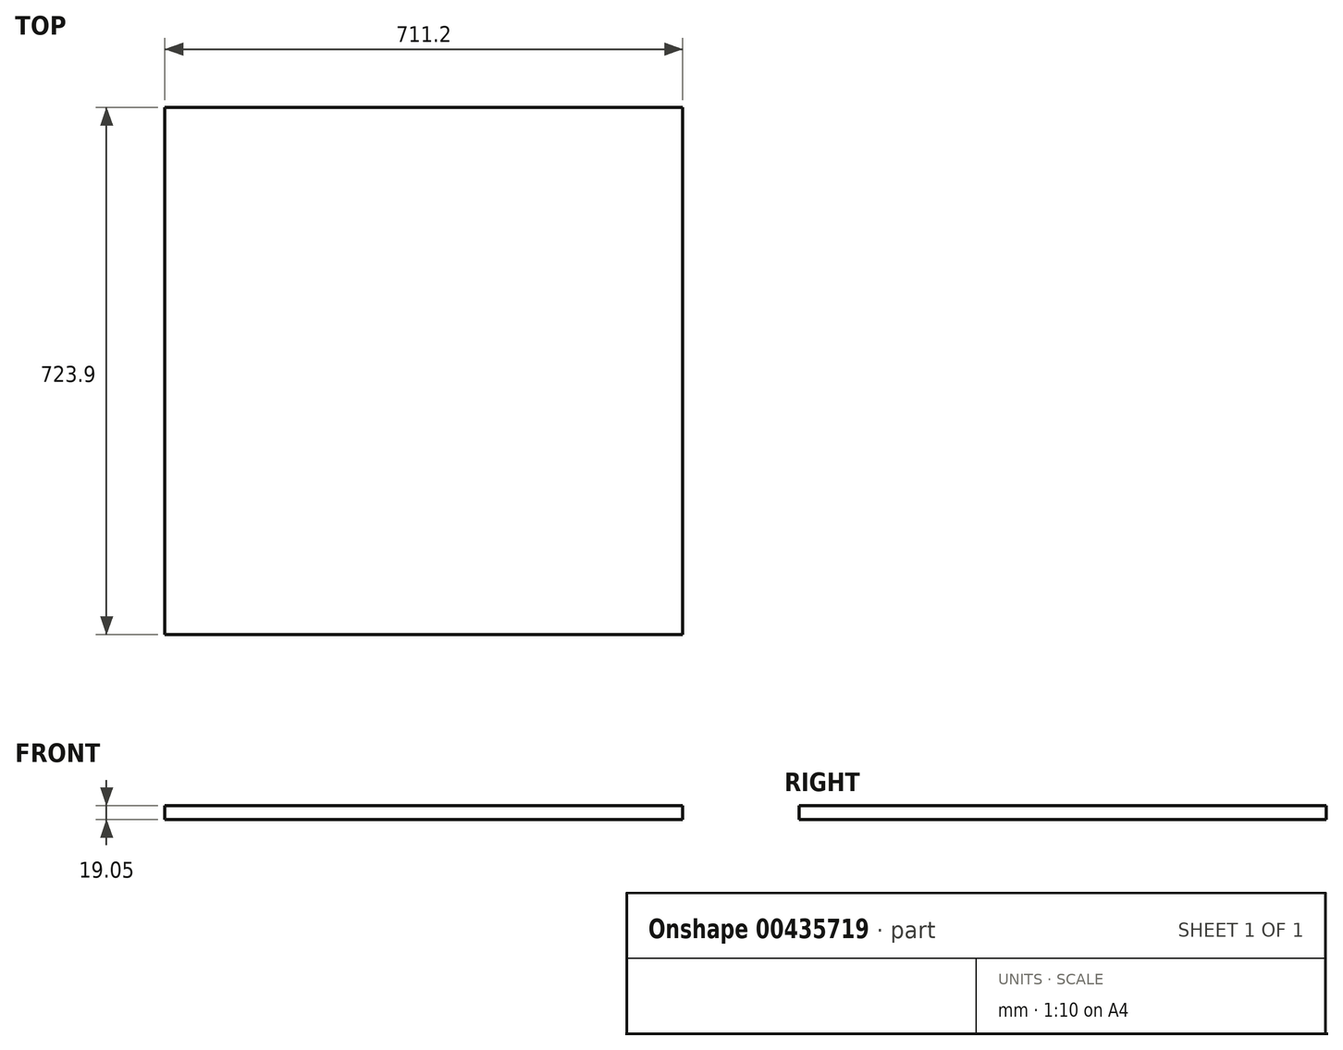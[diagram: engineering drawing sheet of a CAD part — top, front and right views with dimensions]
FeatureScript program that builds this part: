
annotation { "Feature Type Name" : "Feature", "Feature Type Description" : "" }
export const myFeature = defineFeature(function(context is Context, id is Id, definition is map)
    precondition{}
    {
        {
            var Q0;
            Q0=qCreatedBy(makeId("Top.planeOp"),FACE);
            var sketch = newSketch(context, id + "F0", { "sketchPlane" : qUnion([Q0])});
            skLineSegment(sketch, "E0.bottom", {"start": v(355.6, -361.95) * mm, "end": v(-355.6, -361.95) * mm});
            skLineSegment(sketch, "E0.top", {"start": v(355.6, 361.95) * mm, "end": v(-355.6, 361.95) * mm});
            skLineSegment(sketch, "E0.left", {"start": v(355.6, -361.95) * mm, "end": v(355.6, 361.95) * mm});
            skLineSegment(sketch, "E0.right", {"start": v(-355.6, -361.95) * mm, "end": v(-355.6, 361.95) * mm});
            skPoint(sketch, "E0.middle", {"position": v(0, 0) * mm});
            skSolve(sketch);
        }
        {
            var Q0;
            Q0 = qSketchRegion(id + "F0", true);
            extrude(context, id + "F1", {"entities" : qUnion([Q0]), "depth" : 19.05 * mm});
        }
    });
